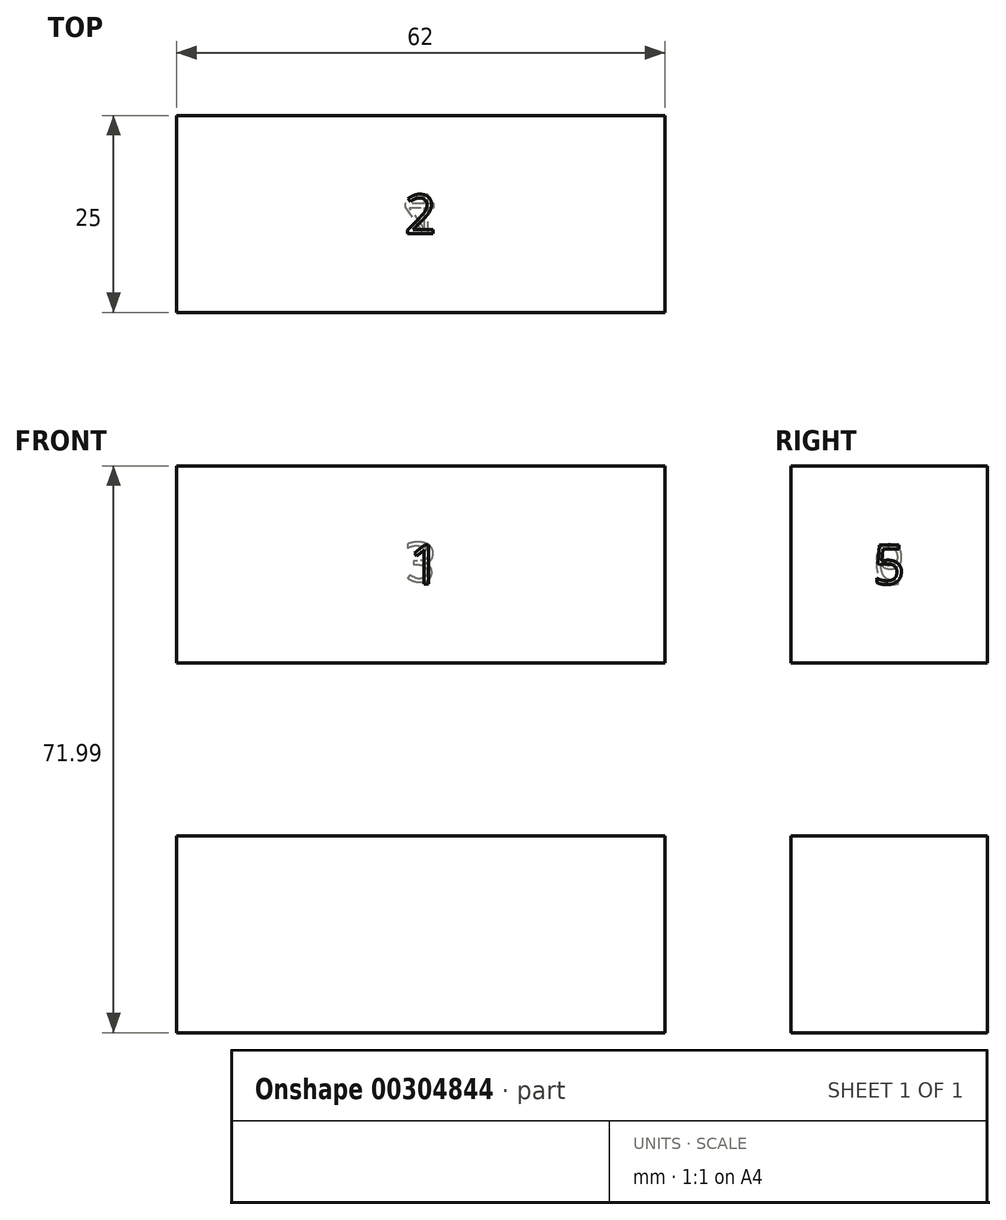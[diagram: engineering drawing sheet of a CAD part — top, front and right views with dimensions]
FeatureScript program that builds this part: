
annotation { "Feature Type Name" : "Feature", "Feature Type Description" : "" }
export const myFeature = defineFeature(function(context is Context, id is Id, definition is map)
    precondition{}
    {
        {
            var Q0;
            Q0=qCreatedBy(makeId("Right.planeOp"),FACE);
            var sketch = newSketch(context, id + "F0", { "sketchPlane" : qUnion([Q0])});
            skLineSegment(sketch, "E0.bottom", {"start": v(-19.43, 44.5) * mm, "end": v(-44.43, 44.5) * mm});
            skLineSegment(sketch, "E0.top", {"start": v(-19.43, 19.5) * mm, "end": v(-44.43, 19.5) * mm});
            skLineSegment(sketch, "E0.left", {"start": v(-19.43, 44.5) * mm, "end": v(-19.43, 19.5) * mm});
            skLineSegment(sketch, "E0.right", {"start": v(-44.43, 44.5) * mm, "end": v(-44.43, 19.5) * mm});
            skLineSegment(sketch, "E1.bottom", {"start": v(-19.43, 91.5) * mm, "end": v(-44.43, 91.5) * mm});
            skLineSegment(sketch, "E1.top", {"start": v(-19.43, 66.5) * mm, "end": v(-44.43, 66.5) * mm});
            skLineSegment(sketch, "E1.left", {"start": v(-19.43, 91.5) * mm, "end": v(-19.43, 66.5) * mm});
            skLineSegment(sketch, "E1.right", {"start": v(-44.43, 91.5) * mm, "end": v(-44.43, 66.5) * mm});
            skSolve(sketch);
        }
        {
            var Q0;
            Q0=makeQuery(id+"F0.imprint","IMPRINT",FACE,{"disambiguationData":[TD([[makeQuery(id+"F0.imprint","IMPRINT",EDGE,{"derivedFrom":sQuery(id+"F0.wireOp",EDGE,"E1.bottom")}),1.0]])]});
            var Q1;
            Q1=makeQuery(id+"F0.imprint","IMPRINT",FACE,{"disambiguationData":[TD([[makeQuery(id+"F0.imprint","IMPRINT",EDGE,{"derivedFrom":sQuery(id+"F0.wireOp",EDGE,"E0.bottom")}),1.0]])]});
            extrude(context, id + "F1", {"entities" : qUnion([Q0, Q1]), "depth" : 62 * mm});
        }
        {
            var Q0;
            Q0=makeQuery(id+"F1.opExtrude","SWEPT_FACE",FACE,{"disambiguationData":[OSD([sQuery(id+"F0.wireOp",EDGE,"E1.right")])]});
            cPlane(context, id + "F2", {"entities" : qUnion([Q0]), "cplaneType" : CPlaneType.OFFSET, "offset" : 0 * mm, "width" : 150 * mm, "height" : 150 * mm});
        }
        {
            var Q0;
            Q0=qCreatedBy(id+"F2.planeOp",FACE);
            var sketch = newSketch(context, id + "F3", { "sketchPlane" : qUnion([Q0])});
            skLineSegment(sketch, "E2", {"start": v(-28.85, 79) * mm, "end": v(-42.4, 79) * mm, "construction": true});
            skLineSegment(sketch, "E3", {"start": v(-28.85, 32) * mm, "end": v(-41.34, 32) * mm, "construction": true});
            skPoint(sketch, "E4", {"position": v(0, 79) * mm});
            skPoint(sketch, "E5", {"position": v(0, 32) * mm});
            skText(sketch, "E6", { "text": "1", "fontName": "OpenSans-Regular.ttf"});
            skText(sketch, "E7", { "text": "2", "fontName": "OpenSans-Regular.ttf"});
            skText(sketch, "E8", { "text": "3", "fontName": "OpenSans-Regular.ttf"});
            skText(sketch, "E9", { "text": "4", "fontName": "OpenSans-Regular.ttf"});
            skText(sketch, "E10", { "text": "5", "fontName": "OpenSans-Regular.ttf"});
            skText(sketch, "E11", { "text": "6", "fontName": "OpenSans-Regular.ttf"});
            skPoint(sketch, "E12", {"position": v(31, 91.5) * mm});
            skPoint(sketch, "E13", {"position": v(29.56, 79) * mm});
            const initialGuessF3  = {"E6": [0.02956, 0.0765, 1, 0, 0.005], "E7": [0.2846, 0.24081, 1, 0, 0.005], "E8": [0.22004, 0.29508, 1, 0, 0.005], "E9": [0.3085, 0.31826, 1, 0, 0.005], "E10": [0.2687, 0.26768, 1, 0, 0.005], "E11": [1.98897, 2.60035, 1, 0, 0.005]};
            skSetInitialGuess(sketch, initialGuessF3);
            skSolve(sketch);
        }
        {
            var Q0;
            Q0=makeQuery(id+"F3.imprint","IMPRINT",FACE,{"disambiguationData":[TD([[makeQuery(id+"F3.imprint","IMPRINT",EDGE,{"derivedFrom":sQuery(id+"F3.wireOp",EDGE,"E6.sketch_text.stroke-0")}),-1.0]])]});
            extrude(context, id + "F4", {"entities" : qUnion([Q0]), "operationType" : NewBodyOperationType.REMOVE, "oppositeDirection" : true, "depth" : 0.01 * mm});
        }
        {
            var Q0;
            Q0=makeQuery(id+"F1.opExtrude","SWEPT_FACE",FACE,{"disambiguationData":[OSD([sQuery(id+"F0.wireOp",EDGE,"E1.bottom")])]});
            var sketch = newSketch(context, id + "F5", { "sketchPlane" : qUnion([Q0])});
            skText(sketch, "E14", { "text": "2", "fontName": "OpenSans-Regular.ttf"});
            skText(sketch, "E15", { "text": "3", "fontName": "OpenSans-Regular.ttf"});
            skText(sketch, "E16", { "text": "4", "fontName": "OpenSans-Regular.ttf"});
            skText(sketch, "E17", { "text": "5", "fontName": "OpenSans-Regular.ttf"});
            skPoint(sketch, "E18", {"position": v(0, -31.93) * mm});
            skPoint(sketch, "E19", {"position": v(28.98, -31.93) * mm});
            const initialGuessF5  = {"E14": [0.02898, -0.03443, 1, 0, 0.005], "E15": [0.07816, 0.11627, 1, 0, 0.005], "E16": [0.16662, 0.13945, 1, 0, 0.005], "E17": [0.12682, 0.08887, 1, 0, 0.005]};
            skSetInitialGuess(sketch, initialGuessF5);
            skSolve(sketch);
        }
        {
            var Q0;
            Q0 = qSketchRegion(id + "F5", true);
            extrude(context, id + "F6", {"entities" : qUnion([Q0]), "operationType" : NewBodyOperationType.REMOVE, "oppositeDirection" : true, "depth" : 0.01 * mm});
        }
        {
            var Q0;
            Q0=makeQuery(id+"F1.opExtrude","SWEPT_FACE",FACE,{"disambiguationData":[OSD([sQuery(id+"F0.wireOp",EDGE,"E1.left")])]});
            var sketch = newSketch(context, id + "F7", { "sketchPlane" : qUnion([Q0])});
            skText(sketch, "E20", { "text": "2", "fontName": "OpenSans-Regular.ttf"});
            skText(sketch, "E21", { "text": "3", "fontName": "OpenSans-Regular.ttf"});
            skText(sketch, "E22", { "text": "4", "fontName": "OpenSans-Regular.ttf"});
            skText(sketch, "E23", { "text": "5", "fontName": "OpenSans-Regular.ttf"});
            skPoint(sketch, "E24", {"position": v(-62, 79) * mm});
            skPoint(sketch, "E25", {"position": v(-31, 91.5) * mm});
            skPoint(sketch, "E26", {"position": v(-33, 79) * mm});
            const initialGuessF7  = {"E20": [0.4197, 0.40788, 1, 0, 0.005], "E21": [-0.029, 0.08177, -1, 0, 0.005], "E22": [0.44359, 0.48533, 1, 0, 0.005], "E23": [0.4038, 0.43475, 1, 0, 0.005]};
            skSetInitialGuess(sketch, initialGuessF7);
            skSolve(sketch);
        }
        {
            var Q0;
            Q0=makeQuery(id+"F1.opExtrude","SWEPT_FACE",FACE,{"disambiguationData":[OSD([sQuery(id+"F0.wireOp",EDGE,"E1.top")])]});
            var sketch = newSketch(context, id + "F8", { "sketchPlane" : qUnion([Q0])});
            skPoint(sketch, "E27", {"position": v(62, 31.93) * mm});
            skPoint(sketch, "E28", {"position": v(31, 19.43) * mm});
            skText(sketch, "E29", { "text": "2", "fontName": "OpenSans-Regular.ttf"});
            skText(sketch, "E30", { "text": "3", "fontName": "OpenSans-Regular.ttf"});
            skText(sketch, "E31", { "text": "4", "fontName": "OpenSans-Regular.ttf"});
            skText(sketch, "E32", { "text": "5", "fontName": "OpenSans-Regular.ttf"});
            skPoint(sketch, "E33", {"position": v(33.14, 31.93) * mm});
            const initialGuessF8  = {"E29": [-0.37753, -0.25097, -1, 0, 0.005], "E30": [-0.31296, -0.30524, -1, 0, 0.005], "E31": [0.02886, 0.02943, 1, 0, 0.005], "E32": [-0.36163, -0.27784, -1, 0, 0.005]};
            skSetInitialGuess(sketch, initialGuessF8);
            skSolve(sketch);
        }
        {
            var Q0;
            Q0 = qSketchRegion(id + "F8", true);
            extrude(context, id + "F9", {"entities" : qUnion([Q0]), "operationType" : NewBodyOperationType.REMOVE, "oppositeDirection" : true, "depth" : 0.01 * mm});
        }
        {
            var Q0;
            Q0=makeQuery(id+"F7.imprint","IMPRINT",FACE,{"disambiguationData":[TD([[makeQuery(id+"F7.imprint","IMPRINT",EDGE,{"derivedFrom":sQuery(id+"F7.wireOp",EDGE,"E21.sketch_text.stroke-0")}),-1.0]])]});
            extrude(context, id + "F10", {"entities" : qUnion([Q0]), "operationType" : NewBodyOperationType.REMOVE, "oppositeDirection" : true, "depth" : 0.01 * mm});
        }
        {
            var Q0;
            Q0=makeQuery(id+"F1.opExtrude","CAP_FACE",FACE,{"disambiguationData":[OSD([sQuery(id+"F0.wireOp",EDGE,"E1.bottom"),sQuery(id+"F0.wireOp",EDGE,"E1.top"),sQuery(id+"F0.wireOp",EDGE,"E1.left"),sQuery(id+"F0.wireOp",EDGE,"E1.right")])],"isStart":false});
            var sketch = newSketch(context, id + "F11", { "sketchPlane" : qUnion([Q0])});
            skText(sketch, "E34", { "text": "6", "fontName": "OpenSans-Regular.ttf"});
            const initialGuessF11  = {"E34": [-0.05799, 0.04564, -1, 0, 0.005]};
            skSetInitialGuess(sketch, initialGuessF11);
            skSolve(sketch);
        }
        {
            var Q0;
            Q0=makeQuery(id+"F11.imprint","IMPRINT",FACE,{"disambiguationData":[TD([[makeQuery(id+"F11.imprint","IMPRINT",EDGE,{"derivedFrom":makeQuery(id+"F1.opExtrude","CAP_EDGE",EDGE,{"disambiguationData":[OSD([sQuery(id+"F0.wireOp",EDGE,"E1.bottom")])],"isStart":false})}),1.0]])]});
            var sketch = newSketch(context, id + "F12", { "sketchPlane" : qUnion([Q0])});
            skText(sketch, "E35", { "text": "5", "fontName": "OpenSans-Regular.ttf"});
            skPoint(sketch, "E36", {"position": v(-31.93, 91.5) * mm});
            skPoint(sketch, "E37", {"position": v(-44.43, 79) * mm});
            skPoint(sketch, "E38", {"position": v(-33.94, 79) * mm});
            const initialGuessF12  = {"E35": [-0.03394, 0.0765, 1, 0, 0.005]};
            skSetInitialGuess(sketch, initialGuessF12);
            skSolve(sketch);
        }
        {
            var Q0;
            Q0 = qSketchRegion(id + "F12", true);
            extrude(context, id + "F13", {"entities" : qUnion([Q0]), "operationType" : NewBodyOperationType.REMOVE, "oppositeDirection" : true, "depth" : 0.01 * mm});
        }
        {
            var Q0;
            Q0=makeQuery(id+"F1.opExtrude","CAP_FACE",FACE,{"disambiguationData":[OSD([sQuery(id+"F0.wireOp",EDGE,"E1.bottom"),sQuery(id+"F0.wireOp",EDGE,"E1.top"),sQuery(id+"F0.wireOp",EDGE,"E1.left"),sQuery(id+"F0.wireOp",EDGE,"E1.right")])],"isStart":true});
            var sketch = newSketch(context, id + "F14", { "sketchPlane" : qUnion([Q0])});
            skText(sketch, "E39", { "text": "6", "fontName": "OpenSans-Regular.ttf"});
            skPoint(sketch, "E40", {"position": v(31.93, 91.5) * mm});
            skPoint(sketch, "E41", {"position": v(19.43, 79) * mm});
            skPoint(sketch, "E42", {"position": v(29.89, 79) * mm});
            const initialGuessF14  = {"E39": [0.03397, 0.0815, -1, 0, 0.005]};
            skSetInitialGuess(sketch, initialGuessF14);
            skSolve(sketch);
        }
        {
            var Q0;
            Q0 = qSketchRegion(id + "F14", true);
            extrude(context, id + "F15", {"entities" : qUnion([Q0]), "operationType" : NewBodyOperationType.REMOVE, "oppositeDirection" : true, "depth" : 0.01 * mm});
        }
    });
